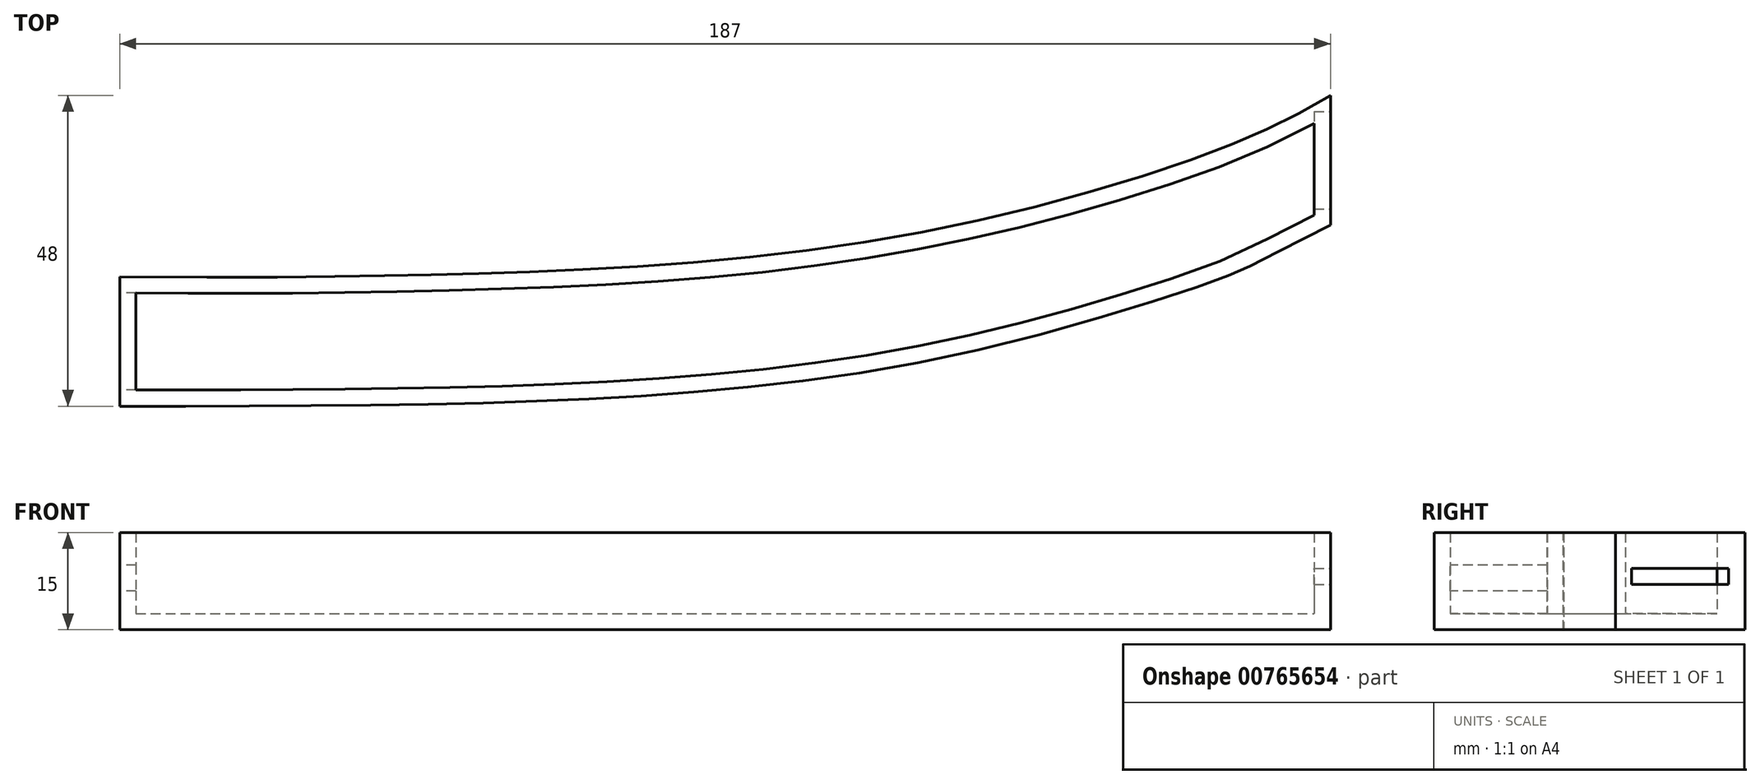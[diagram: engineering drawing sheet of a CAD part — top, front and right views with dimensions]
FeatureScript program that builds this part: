
annotation { "Feature Type Name" : "Feature", "Feature Type Description" : "" }
export const myFeature = defineFeature(function(context is Context, id is Id, definition is map)
    precondition{}
    {
        {
            var Q0;
            Q0=qCreatedBy(makeId("Top.planeOp"),FACE);
            var sketch = newSketch(context, id + "F0", { "sketchPlane" : qUnion([Q0])});
            skPoint(sketch, "E0.1.internal.orphan", {"position": v(50.7, 20.4) * mm});
            skPoint(sketch, "E0.2.internal.orphan", {"position": v(88.7, 22.2) * mm});
            skPoint(sketch, "E0.3.internal.orphan", {"position": v(170.2, 39.8) * mm});
            skPoint(sketch, "E0.5.internal.orphan", {"position": v(187, 48) * mm});
            skPoint(sketch, "E0.start.orphan", {"position": v(0, 20) * mm});
            skFitSpline(sketch, "E1", {"points": [v(0, 20) * mm, v(50.7, 20.4) * mm, v(88.7, 22.2) * mm, v(133, 28.8) * mm, v(170.2, 39.8) * mm, v(187, 48) * mm], "startDerivative": vector(347.02, -2.36) * mm, "endDerivative": vector(116.46, 68.68) * mm});
            skPoint(sketch, "E2.2.internal.orphan", {"position": v(88.8, 2.2) * mm});
            skPoint(sketch, "E2.3.internal.orphan", {"position": v(170.2, 19.8) * mm});
            skPoint(sketch, "E2.5.internal.orphan", {"position": v(187, 28) * mm});
            skPoint(sketch, "E2.start.orphan", {"position": v(0, 0) * mm});
            skFitSpline(sketch, "E3", {"points": [v(0, 0) * mm, v(50.82, 0.4) * mm, v(88.8, 2.2) * mm, v(133, 8.8) * mm, v(170.2, 19.8) * mm, v(187, 28) * mm], "startDerivative": vector(237.12, 0) * mm, "endDerivative": vector(251.55, 125.58) * mm});
            skLineSegment(sketch, "E4", {"start": v(187, 48) * mm, "end": v(187, 28) * mm});
            skLineSegment(sketch, "E5", {"start": v(0, 20) * mm, "end": v(0, 0) * mm});
            skSolve(sketch);
        }
        {
            var Q0;
            Q0=makeQuery(id+"F0.imprint","IMPRINT",FACE,{"disambiguationData":[TD([[makeQuery(id+"F0.imprint","IMPRINT",EDGE,{"derivedFrom":sQuery(id+"F0.wireOp",EDGE,"E1")}),-1.0]])]});
            extrude(context, id + "F1", {"entities" : qUnion([Q0]), "depth" : 15 * mm, "offsetDistance" : 25 * mm});
        }
        {
            var Q0;
            Q0=makeQuery(id+"F1.opExtrude","CAP_FACE",FACE,{"disambiguationData":[OSD([sQuery(id+"F0.wireOp",EDGE,"E1"),sQuery(id+"F0.wireOp",EDGE,"E3"),sQuery(id+"F0.wireOp",EDGE,"E4"),sQuery(id+"F0.wireOp",EDGE,"E5")])],"isStart":false});
            shell(context, id + "F2", {"entities" : qUnion([Q0]), "thickness" : 2.5 * mm});
        }
        {
            var Q0;
            Q0=makeQuery(id+"F1.opExtrude","SWEPT_FACE",FACE,{"disambiguationData":[OSD([sQuery(id+"F0.wireOp",EDGE,"E5")])]});
            var sketch = newSketch(context, id + "F3", { "sketchPlane" : qUnion([Q0])});
            skLineSegment(sketch, "E6.bottom", {"start": v(-17.5, 10) * mm, "end": v(-2.5, 10) * mm});
            skLineSegment(sketch, "E6.top", {"start": v(-17.5, 6) * mm, "end": v(-2.5, 6) * mm});
            skLineSegment(sketch, "E6.left", {"start": v(-17.5, 10) * mm, "end": v(-17.5, 6) * mm});
            skLineSegment(sketch, "E6.right", {"start": v(-2.5, 10) * mm, "end": v(-2.5, 6) * mm});
            skSolve(sketch);
        }
        {
            var Q0;
            Q0=qSketchRegion(id+"F3",true);
            var Q1;
            Q1=makeQuery(id+"F2.opShell","OFFSET_FACE",FACE,{"disambiguationData":[OSD([sQuery(id+"F0.wireOp",EDGE,"E5")])]});
            extrude(context, id + "F4", {"entities" : qUnion([Q0]), "operationType" : NewBodyOperationType.REMOVE, "endBound" : BoundingType.UP_TO_SURFACE, "oppositeDirection" : true, "depth" : 25 * mm, "endBoundEntityFace" : qUnion([Q1]), "offsetDistance" : 25 * mm});
        }
        {
            var Q0;
            Q0=makeQuery(id+"F1.opExtrude","SWEPT_FACE",FACE,{"disambiguationData":[OSD([sQuery(id+"F0.wireOp",EDGE,"E4")])]});
            var sketch = newSketch(context, id + "F5", { "sketchPlane" : qUnion([Q0])});
            skLineSegment(sketch, "E7.bottom", {"start": v(30.5, 9.5) * mm, "end": v(45.5, 9.5) * mm});
            skLineSegment(sketch, "E7.top", {"start": v(30.5, 7) * mm, "end": v(45.5, 7) * mm});
            skLineSegment(sketch, "E7.left", {"start": v(30.5, 9.5) * mm, "end": v(30.5, 7) * mm});
            skLineSegment(sketch, "E7.right", {"start": v(45.5, 9.5) * mm, "end": v(45.5, 7) * mm});
            skSolve(sketch);
        }
        {
            var Q0;
            Q0=qSketchRegion(id+"F5",true);
            var Q1;
            Q1=makeQuery(id+"F2.opShell","OFFSET_FACE",FACE,{"disambiguationData":[OSD([sQuery(id+"F0.wireOp",EDGE,"E4")])]});
            extrude(context, id + "F6", {"entities" : qUnion([Q0]), "operationType" : NewBodyOperationType.REMOVE, "endBound" : BoundingType.UP_TO_SURFACE, "oppositeDirection" : true, "depth" : 25 * mm, "endBoundEntityFace" : qUnion([Q1]), "offsetDistance" : 25 * mm});
        }
    });
